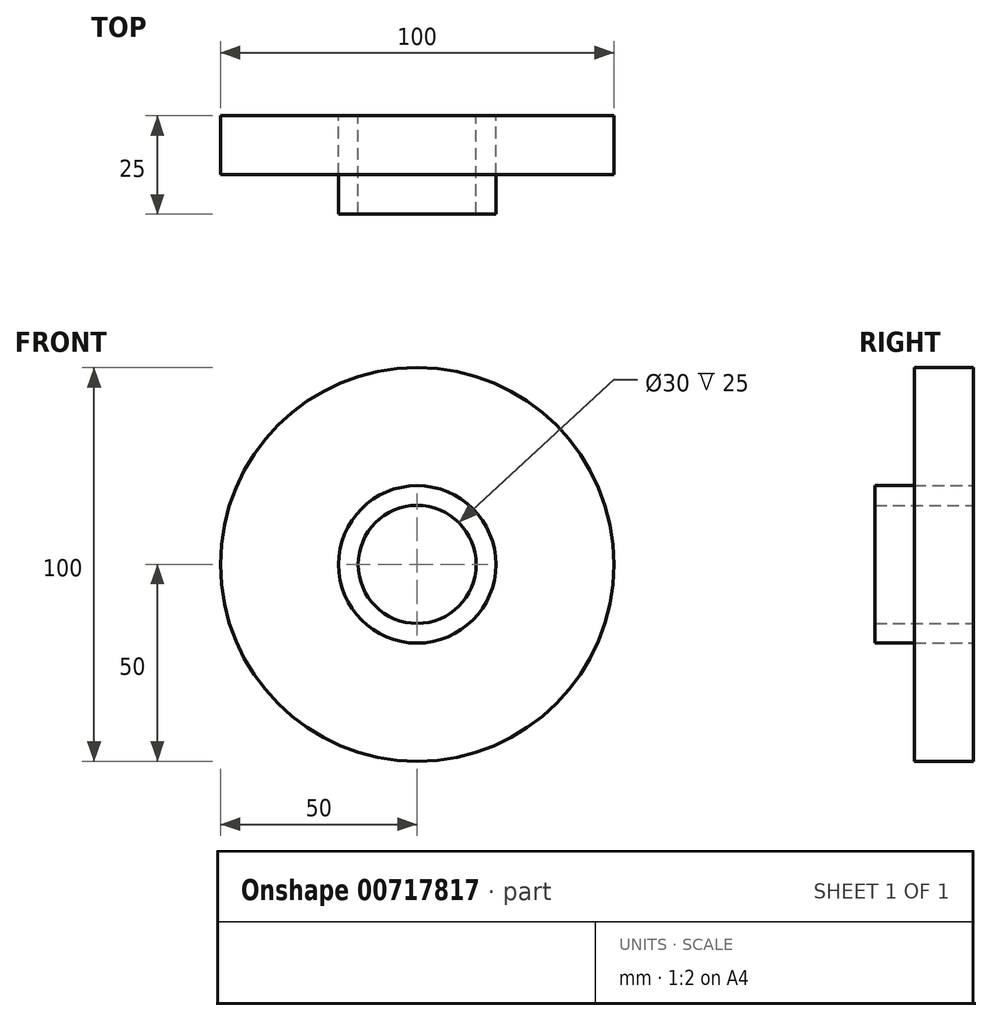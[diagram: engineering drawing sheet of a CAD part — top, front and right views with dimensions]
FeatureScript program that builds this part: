
annotation { "Feature Type Name" : "Feature", "Feature Type Description" : "" }
export const myFeature = defineFeature(function(context is Context, id is Id, definition is map)
    precondition{}
    {
        {
            var Q0;
            Q0=qCreatedBy(makeId("Front.planeOp"),FACE);
            var sketch = newSketch(context, id + "F0", { "sketchPlane" : qUnion([Q0])});
            skCircle(sketch, "E0", {"center": v(0, 0) * mm, "radius": 50 * mm});
            skSolve(sketch);
        }
        {
            var Q0;
            Q0=makeQuery(id+"F0.imprint","IMPRINT",FACE,{"disambiguationData":[TD([[makeQuery(id+"F0.imprint","IMPRINT",EDGE,{"derivedFrom":sQuery(id+"F0.wireOp",EDGE,"E0")}),1.0]])]});
            extrude(context, id + "F1", {"entities" : qUnion([Q0]), "depth" : 15 * mm, "offsetDistance" : 25 * mm});
        }
        {
            var Q0;
            Q0=qCreatedBy(makeId("Front.planeOp"),FACE);
            var sketch = newSketch(context, id + "F2", { "sketchPlane" : qUnion([Q0])});
            skCircle(sketch, "E1", {"center": v(0, 0) * mm, "radius": 15 * mm});
            skSolve(sketch);
        }
        {
            var Q0;
            Q0=qCreatedBy(makeId("Front.planeOp"),FACE);
            var sketch = newSketch(context, id + "F3", { "sketchPlane" : qUnion([Q0])});
            skCircle(sketch, "E2", {"center": v(0, 0) * mm, "radius": 20 * mm});
            skSolve(sketch);
        }
        {
            var Q0;
            Q0=makeQuery(id+"F3.imprint","IMPRINT",FACE,{"disambiguationData":[TD([[makeQuery(id+"F3.imprint","IMPRINT",EDGE,{"derivedFrom":sQuery(id+"F3.wireOp",EDGE,"E2")}),1.0]])]});
            var Q1;
            Q1=makeQuery(id+"F2.imprint","IMPRINT",FACE,{"disambiguationData":[TD([[makeQuery(id+"F2.imprint","IMPRINT",EDGE,{"derivedFrom":sQuery(id+"F2.wireOp",EDGE,"E1")}),1.0]])]});
            extrude(context, id + "F4", {"entities" : qUnion([Q0, Q1]), "depth" : 25 * mm, "offsetDistance" : 25 * mm});
        }
        {
            var Q0;
            Q0=makeQuery(id+"F4.opExtrude","SWEPT_BODY",BODY,{"disambiguationData":[OSD([sQuery(id+"F2.wireOp",EDGE,"E1")])]});
            var Q1;
            Q1=makeQuery(id+"F4.opExtrude","SWEPT_BODY",BODY,{"disambiguationData":[OSD([sQuery(id+"F3.wireOp",EDGE,"E2")])]});
            booleanBodies(context, id + "F5", {"operationType" : BooleanOperationType.SUBTRACTION, "tools" : qUnion([Q0]), "targets" : qUnion([Q1])});
        }
    });
